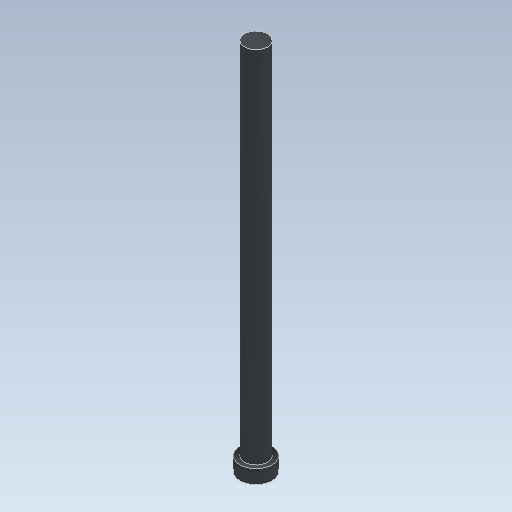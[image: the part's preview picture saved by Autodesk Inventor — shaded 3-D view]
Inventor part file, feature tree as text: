
AUTODESK INVENTOR PART (.ipt)
format: ipt  version: 2021 (Build 250183000, 183)  size: 97,792 bytes
history: native  units: mm
features: extrude x2, sketch x2, other x1
ambient origin geometry x8: Origin, YZ Plane, XZ Plane, XY Plane, X Axis, Y Axis, Z Axis, Center Point
bodies: Body1 (feature_tree)
feature tree (5):
  other  "Sólido1"
  extrude  "Extrusión1"  Depth=78.0mm
  extrude  "Extrusión2"  [1 undecoded]
  sketch  "Boceto1"  dims[d1=78.0mm d2=0.0mm d3=7.0mm]
  sketch  "Boceto2"  dims[d4=3.0mm d5=0.0mm]
note: 1 required parameter value undecoded (feature->parameter linkage not recoverable at this tier; creation-order binding heuristic only, values carry confidence <= 0.55)
